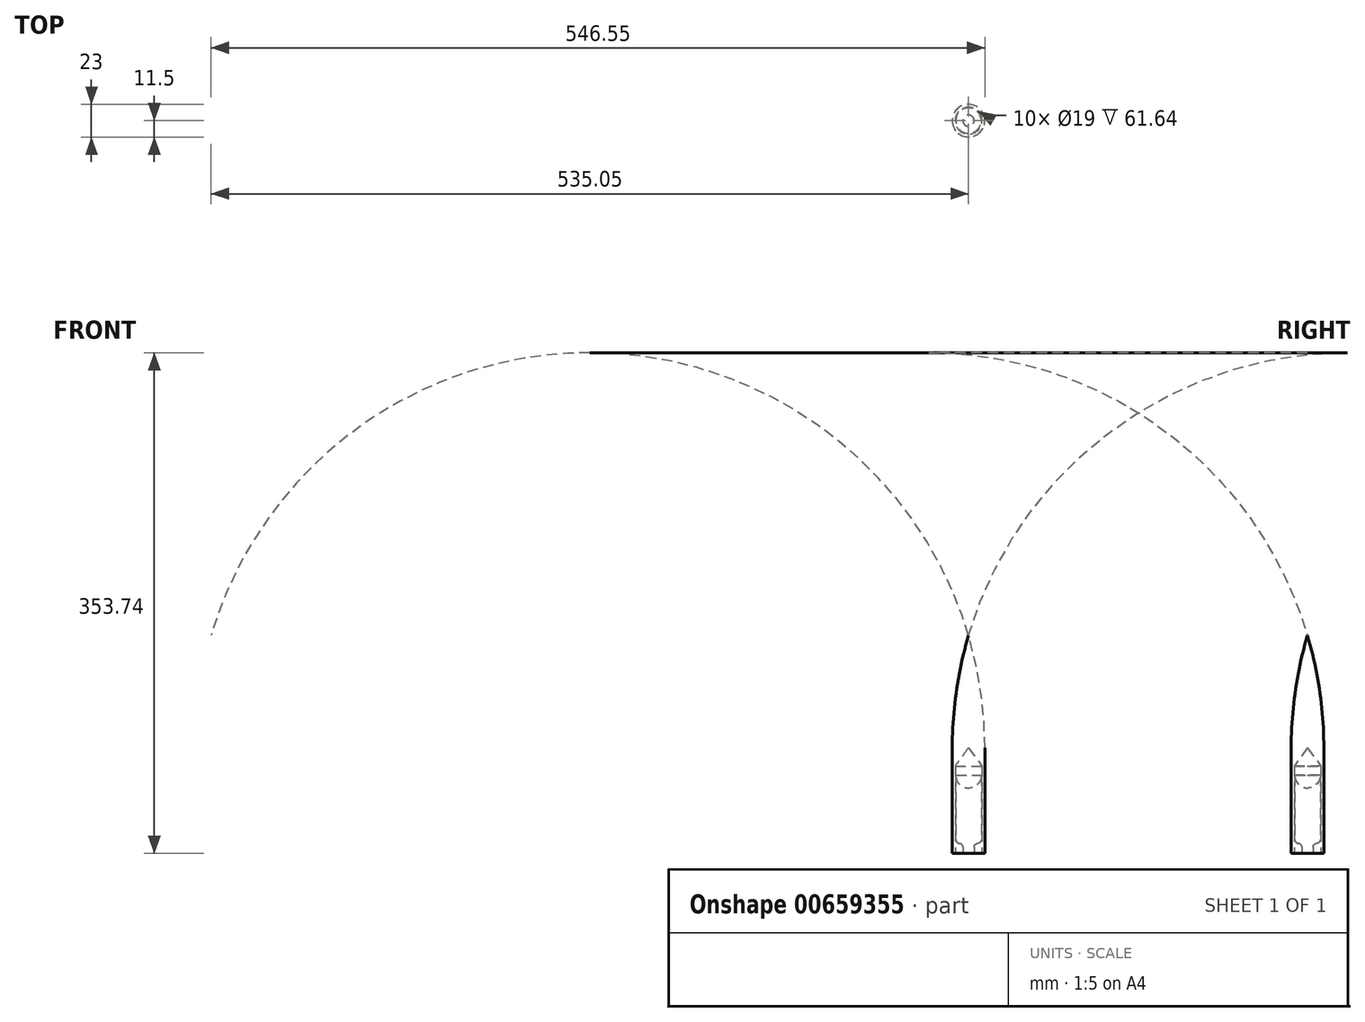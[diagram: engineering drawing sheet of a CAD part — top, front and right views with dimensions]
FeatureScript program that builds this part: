
annotation { "Feature Type Name" : "Feature", "Feature Type Description" : "" }
export const myFeature = defineFeature(function(context is Context, id is Id, definition is map)
    precondition{}
    {
        {
            var Q0;
            Q0=qCreatedBy(makeId("Right.planeOp"),FACE);
            var sketch = newSketch(context, id + "F0", { "sketchPlane" : qUnion([Q0])});
            skLineSegment(sketch, "E0", {"start": v(0, 0) * mm, "end": v(0, 64) * mm});
            skLineSegment(sketch, "E1", {"start": v(9, 9.8) * mm, "end": v(9, 55.08) * mm});
            skLineSegment(sketch, "E2", {"start": v(0, 0) * mm, "end": v(4, 0) * mm});
            skLineSegment(sketch, "E3", {"start": v(4, 0) * mm, "end": v(4, 4.44) * mm});
            skArc(sketch, "E4", {"start": v(9, 55.08) * mm, "mid": v(6.36, 61.42) * mm, "end": v(0, 64) * mm});
            skArc(sketch, "E5", {"start": v(6.34, 6.95) * mm, "mid": v(8.23, 7.85) * mm, "end": v(9, 9.8) * mm});
            skArc(sketch, "E6", {"start": v(6.34, 6.95) * mm, "mid": v(4.68, 6.15) * mm, "end": v(4, 4.44) * mm});
            skSolve(sketch);
        }
        {
            var Q0;
            Q0=makeQuery(id+"F0.imprint","IMPRINT",FACE,{"disambiguationData":[TD([[makeQuery(id+"F0.imprint","IMPRINT",EDGE,{"derivedFrom":sQuery(id+"F0.wireOp",EDGE,"E0")}),-1.0]])]});
            var Q1;
            Q1=sQuery(id+"F0.wireOp",EDGE,"E0");
            revolve(context, id + "F1", {"entities" : qUnion([Q0]), "axis" : qUnion([Q1]), "revolveType" : RevolveType.FULL});
        }
        {
            var Q0;
            Q0=qCreatedBy(makeId("Right.planeOp"),FACE);
            var sketch = newSketch(context, id + "F2", { "sketchPlane" : qUnion([Q0])});
            skLineSegment(sketch, "E7", {"start": v(0, 0) * mm, "end": v(0, 45.43) * mm});
            skLineSegment(sketch, "E8", {"start": v(9.5, 0) * mm, "end": v(9.5, 61.64) * mm});
            skLineSegment(sketch, "E9", {"start": v(9.5, 61.64) * mm, "end": v(0, 74.72) * mm});
            skLineSegment(sketch, "E10", {"start": v(9.5, 0) * mm, "end": v(11.5, 0) * mm});
            skLineSegment(sketch, "E11", {"start": v(11.5, 0) * mm, "end": v(11.5, 74.72) * mm});
            skLineSegment(sketch, "E12", {"start": v(0, 45.43) * mm, "end": v(0, 154) * mm});
            skArc(sketch, "E13", {"start": v(11.5, 74.72) * mm, "mid": v(8.61, 114.77) * mm, "end": v(0, 154) * mm});
            skSolve(sketch);
        }
        {
            var Q0;
            Q0=makeQuery(id+"F2.imprint","IMPRINT",FACE,{"disambiguationData":[TD([[makeQuery(id+"F2.imprint","IMPRINT",EDGE,{"derivedFrom":sQuery(id+"F2.wireOp",EDGE,"E8")}),-1.0]])]});
            var Q1;
            Q1=sQuery(id+"F2.wireOp",EDGE,"E12");
            revolve(context, id + "F3", {"entities" : qUnion([Q0]), "axis" : qUnion([Q1]), "revolveType" : RevolveType.FULL});
        }
    });
